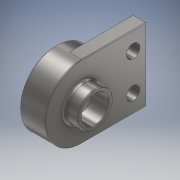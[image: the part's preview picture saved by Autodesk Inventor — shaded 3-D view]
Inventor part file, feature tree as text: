
AUTODESK INVENTOR PART (.ipt)
format: ipt  version: 2018 (Build 220112000, 112)  size: 204,800 bytes
history: native  units: mm
features: sketch x3, chamfer x2, revolve x1, fillet x1, extrude x1, hole x1
ambient origin geometry x8: Origin, YZ Plane, XZ Plane, XY Plane, X Axis, Y Axis, Z Axis, Center Point
bodies: Body1 (feature_tree)
feature tree (9):
  revolve  "Rivoluzione1"
  fillet  "Raccordo1"  Radius=20.0mm
  chamfer  "Smusso1"  Distance=26.0mm
  extrude  "Estrusione3"  Depth=10.0mm
  chamfer  "Smusso2"  Distance=47.0mm
  hole  "Foro1"  [1 undecoded]
  sketch  "Schizzo3"
  sketch  "Schizzo4"
  sketch  "Schizzo5"
note: 1 required parameter value undecoded (feature->parameter linkage not recoverable at this tier; creation-order binding heuristic only, values carry confidence <= 0.55)
